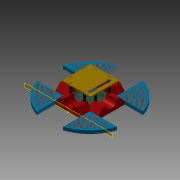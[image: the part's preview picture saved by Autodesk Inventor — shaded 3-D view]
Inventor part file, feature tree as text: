
AUTODESK INVENTOR PART (.ipt)
format: ipt  version: 2015 (Build 190159000, 159)  size: 1,577,472 bytes
history: native  units: in
note: dims shown in document units (in); Inventor stores cm internally (conversion verified against a paired STEP export)
features: other x9, sketch x3, plane x2
ambient origin geometry x8: Origin, YZ Plane, XZ Plane, XY Plane, X Axis, Y Axis, Z Axis, Center Point
bodies: Solid6 (feature_tree), Solid8 (feature_tree), Solid9 (feature_tree)
feature tree (14):
  other  "roundBase.ipt"
  other  "Solid1::roundBase.ipt_1"
  other  "TaggingFeature6"
  plane  "Work Plane1_1"
  other  "Solid1::roundBase.ipt"
  other  "TaggingFeature7"
  sketch  "Sketch7"  dims[d7=1.1811in d8=1.1811in]
  other  "Solid1::roundBase.ipt_2"
  other  "TaggingFeature8"
  sketch  "Sketch7_1"  dims[d5=1.1811in]
  plane  "Work Plane1_2"
  other  "Solid1::roundBase.ipt_3"
  other  "TaggingFeature9"
  sketch  "Sketch7_2"  dims[d6=1.1811in]
